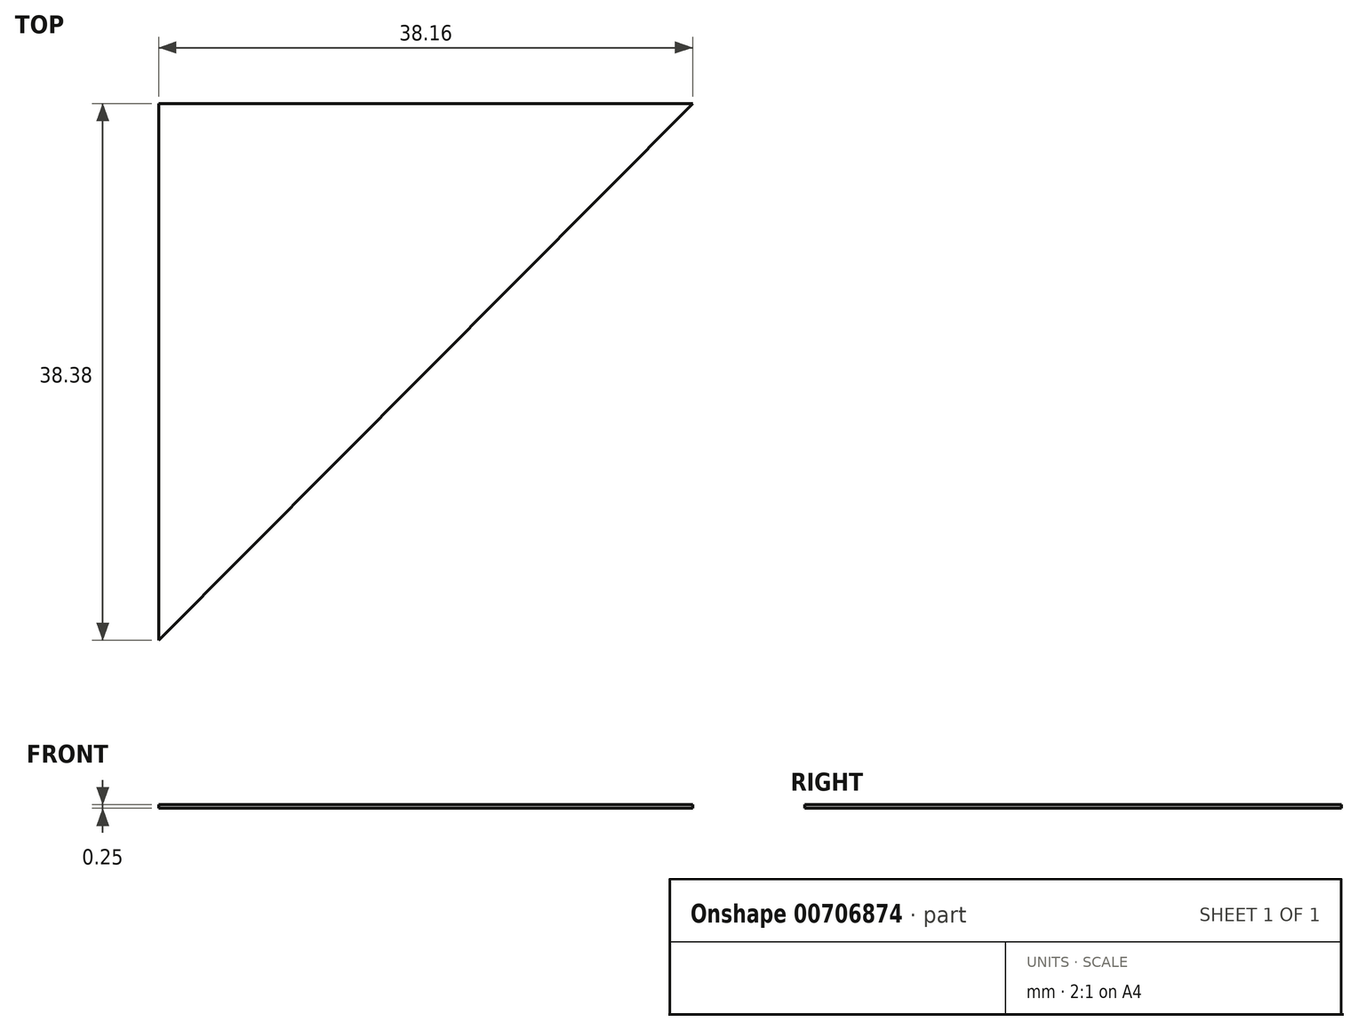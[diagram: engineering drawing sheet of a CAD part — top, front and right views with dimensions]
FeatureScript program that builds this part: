
annotation { "Feature Type Name" : "Feature", "Feature Type Description" : "" }
export const myFeature = defineFeature(function(context is Context, id is Id, definition is map)
    precondition{}
    {
        {
            var Q0;
            Q0=qCreatedBy(makeId("Top.planeOp"),FACE);
            var sketch = newSketch(context, id + "F0", { "sketchPlane" : qUnion([Q0])});
            skLineSegment(sketch, "E0", {"start": v(-44.43, -8.78) * mm, "end": v(-82.6, -8.78) * mm});
            skLineSegment(sketch, "E1", {"start": v(-82.6, -8.78) * mm, "end": v(-82.6, -47.16) * mm});
            skLineSegment(sketch, "E2", {"start": v(-82.6, -47.16) * mm, "end": v(-44.43, -8.78) * mm});
            skSolve(sketch);
        }
        {
            var Q0;
            Q0 = qSketchRegion(id + "F0", true);
            extrude(context, id + "F1", {"entities" : qUnion([Q0]), "depth" : 0.25 * mm, "offsetDistance" : 25.4 * mm});
        }
    });
